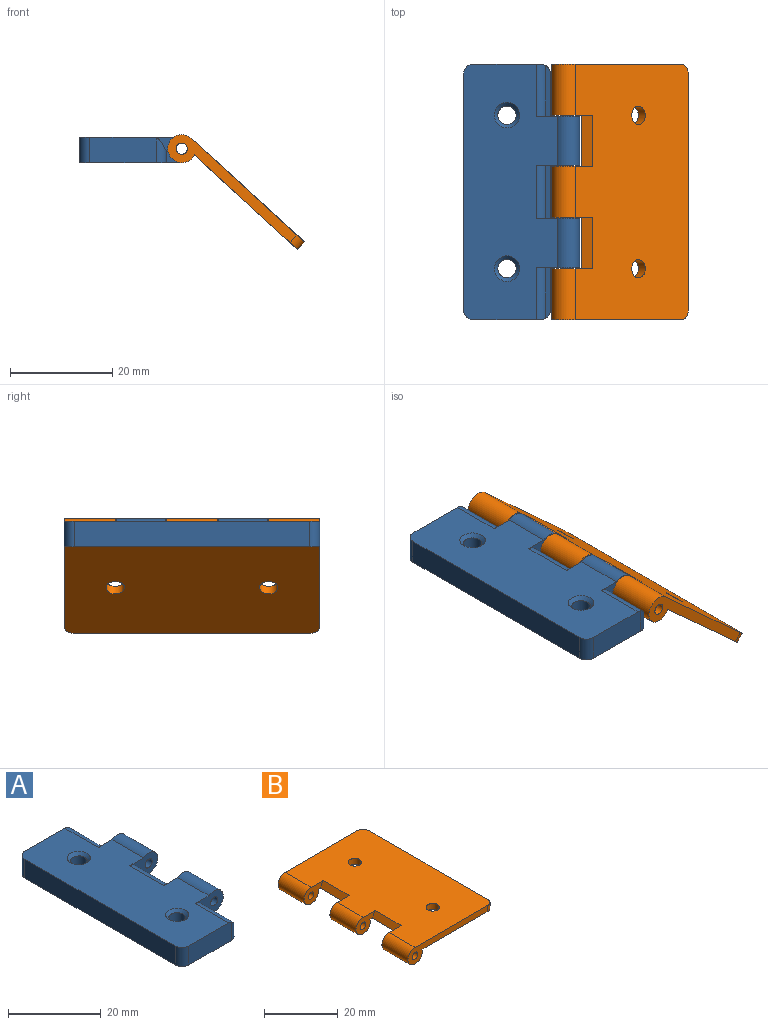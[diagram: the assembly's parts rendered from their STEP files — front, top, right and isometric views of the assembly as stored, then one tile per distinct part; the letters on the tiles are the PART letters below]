
ASSEMBLY  parts=2 mates=2
PART A: 30 faces, bbox 22.8x50x5.5 mm
  f0: plane 8.2x2.25mm, normal (1,0,0), area 18.5mm2, adj f5,f15,f22,f23
  f1: plane 10.4x2.25mm, normal (1,0,0), area 23.4mm2, adj f5,f10,f11,f21
  f2: plane 50x18.42mm, normal (0,0,1), area 751.8mm2, adj f3,f6,f7,f8,f9,f10,f11,f13
  f3: plane 13x5mm, normal (0,-1,0), area 65mm2, adj f2,f5,f26,f27,f29
  f4: cylinder r=1.8mm len=4.3mm, axis (0,0,1), area 48.6mm2, adj f5,f19
  f5: plane 50x20mm, normal (0,0,-1), area 883.8mm2, adj f0,f1,f3,f4,f6,f7,f8,f9
  f6: cylinder r=2.75mm len=9.6mm, axis (0,1,0), area 99.1mm2, adj f2,f5,f10,f15
  f7: plane 13x5mm, normal (0,1,0), area 65mm2, adj f2,f5,f23,f24,f28
  f8: cylinder r=2.75mm len=9.6mm, axis (0,1,0), area 99.1mm2, adj f2,f5,f11,f13
  f9: plane 46x5mm, normal (-1,0,0), area 230mm2, adj f2,f5,f28,f29
  f10: plane 8.49x5.5mm, normal (0,-1,0), area 26mm2, adj f1,f2,f5,f6,f16,f21,f25
  f11: plane 8.49x5.5mm, normal (0,1,0), area 26mm2, adj f1,f2,f5,f8,f12,f21,f25
  f12: cylinder r=1.1mm len=9.6mm, axis (0,1,0), area 66.4mm2, adj f11,f13
  f13: plane 8.49x5.5mm, normal (0,-1,0), area 26mm2, adj f2,f5,f8,f12,f14,f20,f27
  f14: plane 8.2x2.25mm, normal (1,0,0), area 18.4mm2, adj f5,f13,f20,f26
  f15: plane 8.49x5.5mm, normal (0,1,0), area 26mm2, adj f0,f2,f5,f6,f16,f22,f24
  f16: cylinder r=1.1mm len=9.6mm, axis (0,1,0), area 66.4mm2, adj f10,f15
  f17: cylinder r=1.8mm len=4.3mm, axis (0,0,1), area 48.6mm2, adj f5,f18
  f18: cone r=0mm half-angle=45deg, axis (0,0,1), area 13.4mm2, adj f2,f17
  f19: cone r=3mm half-angle=45deg, axis (0,0,1), area 13.4mm2, adj f2,f4
  f20: plane 9.94x1.75mm, normal (0.87,0,0.5), area 19.1mm2, adj f13,f14,f26,f27
  f21: plane 10.4x1.75mm, normal (0.87,0,0.5), area 21mm2, adj f1,f10,f11,f25
  f22: plane 9.94x1.75mm, normal (0.87,0,0.5), area 19.1mm2, adj f0,f15,f23,f24
  f23: cylinder r=2mm len=4.86mm, axis (0,0,1), area 10.7mm2, adj f0,f5,f7,f22,f24
  f24: cylinder r=2mm len=10.2mm, axis (0,-1,0), area 21.2mm2, adj f2,f7,f15,f22,f23
  f25: cylinder r=2mm len=10.4mm, axis (0,-1,0), area 21.8mm2, adj f2,f10,f11,f21
  f26: cylinder r=2mm len=4.86mm, axis (0,0,-1), area 10.7mm2, adj f3,f5,f14,f20,f27
  f27: cylinder r=2mm len=10.2mm, axis (0,1,0), area 21.2mm2, adj f2,f3,f13,f20,f26
  f28: cylinder r=2mm len=5mm, axis (0,0,-1), area 15.7mm2, adj f2,f5,f7,f9
  f29: cylinder r=2mm len=5mm, axis (0,0,1), area 15.7mm2, adj f2,f3,f5,f9
PART B: 21 faces, bbox 32.8x50x5.5 mm
  f0: plane 50x30mm, normal (0,0,1), area 1384.8mm2, adj f1,f2,f5,f7,f8,f9,f10,f11
  f1: cylinder r=2.75mm len=10mm, axis (0,1,0), area 137.2mm2, adj f0,f3,f9,f13
  f2: cylinder r=2.75mm len=10mm, axis (0,1,0), area 137.2mm2, adj f0,f3,f11,f14
  f3: plane 50x27.35mm, normal (0,0,-1), area 1328.6mm2, adj f1,f2,f5,f7,f8,f9,f10,f11
  f4: cylinder r=1.1mm len=10mm, axis (0,1,0), area 69.1mm2, adj f9,f13
  f5: cylinder r=2.75mm len=10mm, axis (0,1,0), area 137.2mm2, adj f0,f3,f8,f10
  f6: cylinder r=1.1mm len=10mm, axis (0,1,0), area 69.1mm2, adj f8,f10
  f7: plane 46x2mm, normal (1,0,0), area 92mm2, adj f0,f3,f19,f20
  f8: plane 30.75x5.5mm, normal (0,-1,0), area 72.1mm2, adj f0,f3,f5,f6,f20
  f9: plane 30.75x5.5mm, normal (0,1,0), area 72.1mm2, adj f0,f1,f3,f4,f19
  f10: plane 7.4x5.5mm, normal (0,1,0), area 24.2mm2, adj f0,f3,f5,f6,f18
  f11: plane 7.4x5.5mm, normal (0,-1,0), area 24.2mm2, adj f0,f2,f3,f12,f18
  f12: cylinder r=1.1mm len=10mm, axis (0,1,0), area 69.1mm2, adj f11,f14
  f13: plane 7.4x5.5mm, normal (0,-1,0), area 24.2mm2, adj f0,f1,f3,f4,f17
  f14: plane 7.4x5.5mm, normal (0,1,0), area 24.2mm2, adj f0,f2,f3,f12,f17
  f15: cylinder r=1.8mm len=3.6mm, axis (0,0,1), area 22.6mm2, adj f0,f3
  f16: cylinder r=1.8mm len=3.6mm, axis (0,0,1), area 22.6mm2, adj f0,f3
  f17: plane 10x2mm, normal (-0.87,0,0.5), area 23.1mm2, adj f0,f3,f13,f14
  f18: plane 10x2mm, normal (-0.87,0,0.5), area 23.1mm2, adj f0,f3,f10,f11
  f19: cylinder r=2mm len=2mm, axis (0,0,1), area 6.3mm2, adj f0,f3,f7,f9
  f20: cylinder r=2mm len=2mm, axis (0,0,-1), area 6.3mm2, adj f0,f3,f7,f8
PLACE A t=(21,0,2.75)mm
PLACE B rot(axis=(0,1,0),42.4deg) t=(15.79,0,4.77)mm
MATE planar A.f3 <-> B.f8  axis (0,-1,0) through (6.5,-50,2.5)mm
MATE cylindrical A.f12 <-> B.f4  axis (0,1,0) through (18,-19.8,2.75)mm
